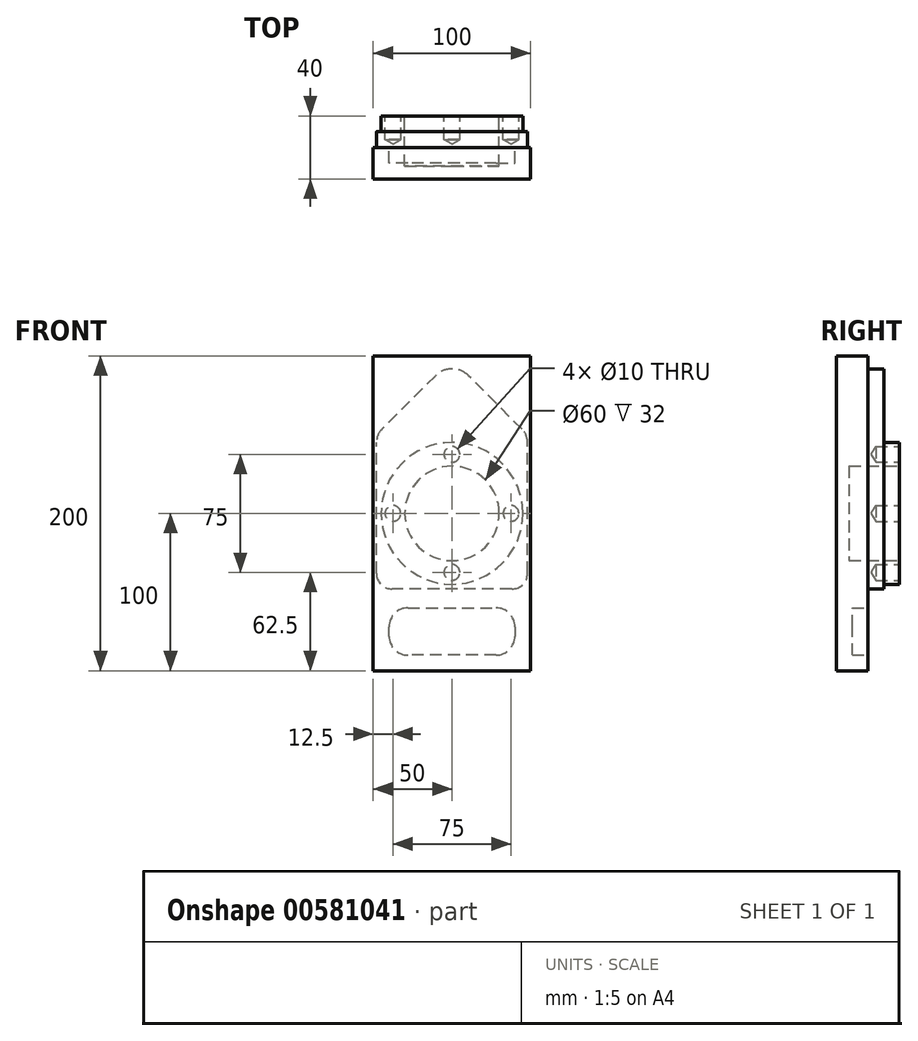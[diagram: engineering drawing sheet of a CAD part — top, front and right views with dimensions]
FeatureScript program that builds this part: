
annotation { "Feature Type Name" : "Feature", "Feature Type Description" : "" }
export const myFeature = defineFeature(function(context is Context, id is Id, definition is map)
    precondition{}
    {
        {
            var Q0;
            Q0=qCreatedBy(makeId("Front.planeOp"),FACE);
            var sketch = newSketch(context, id + "F0", { "sketchPlane" : qUnion([Q0])});
            skLineSegment(sketch, "E0.bottom", {"start": v(50, -100) * mm, "end": v(-50, -100) * mm});
            skLineSegment(sketch, "E0.top", {"start": v(50, 100) * mm, "end": v(-50, 100) * mm});
            skLineSegment(sketch, "E0.left", {"start": v(50, -100) * mm, "end": v(50, 100) * mm});
            skLineSegment(sketch, "E0.right", {"start": v(-50, -100) * mm, "end": v(-50, 100) * mm});
            skPoint(sketch, "E0.middle", {"position": v(0, 0) * mm});
            skSolve(sketch);
        }
        {
            var Q0;
            Q0=makeQuery(id+"F0.imprint","IMPRINT",FACE,{"disambiguationData":[TD([[makeQuery(id+"F0.imprint","IMPRINT",EDGE,{"derivedFrom":sQuery(id+"F0.wireOp",EDGE,"E0.bottom")}),-1.0]])]});
            extrude(context, id + "F1", {"entities" : qUnion([Q0]), "depth" : 20 * mm, "offsetDistance" : 25 * mm});
        }
        {
            var Q0;
            Q0=makeQuery(id+"F1.opExtrude","CAP_FACE",FACE,{"disambiguationData":[OSD([sQuery(id+"F0.wireOp",EDGE,"E0.bottom"),sQuery(id+"F0.wireOp",EDGE,"E0.top"),sQuery(id+"F0.wireOp",EDGE,"E0.left"),sQuery(id+"F0.wireOp",EDGE,"E0.right")])],"isStart":true});
            var sketch = newSketch(context, id + "F2", { "sketchPlane" : qUnion([Q0])});
            skLineSegment(sketch, "E1", {"start": v(-40, -72) * mm, "end": v(-40, -78) * mm});
            skLineSegment(sketch, "E2", {"start": v(-28, -90) * mm, "end": v(28, -90) * mm});
            skLineSegment(sketch, "E3", {"start": v(40, -78) * mm, "end": v(40, -72) * mm});
            skLineSegment(sketch, "E4", {"start": v(28, -60) * mm, "end": v(-28, -60) * mm});
            skArc(sketch, "E5", {"start": v(28, -90) * mm, "mid": v(36.49, -86.49) * mm, "end": v(40, -78) * mm});
            skArc(sketch, "E6", {"start": v(40, -72) * mm, "mid": v(36.49, -63.51) * mm, "end": v(28, -60) * mm});
            skArc(sketch, "E7", {"start": v(-40, -78) * mm, "mid": v(-36.49, -86.49) * mm, "end": v(-28, -90) * mm});
            skArc(sketch, "E8", {"start": v(-28, -60) * mm, "mid": v(-36.49, -63.51) * mm, "end": v(-40, -72) * mm});
            skSolve(sketch);
        }
        {
            var Q0;
            Q0 = qSketchRegion(id + "F2", true);
            extrude(context, id + "F3", {"entities" : qUnion([Q0]), "operationType" : NewBodyOperationType.REMOVE, "oppositeDirection" : true, "depth" : 10 * mm, "offsetDistance" : 25 * mm});
        }
        {
            var Q0;
            Q0=makeQuery(id+"F1.opExtrude","CAP_FACE",FACE,{"disambiguationData":[OSD([sQuery(id+"F0.wireOp",EDGE,"E0.bottom"),sQuery(id+"F0.wireOp",EDGE,"E0.top"),sQuery(id+"F0.wireOp",EDGE,"E0.left"),sQuery(id+"F0.wireOp",EDGE,"E0.right")])],"isStart":true});
            var sketch = newSketch(context, id + "F4", { "sketchPlane" : qUnion([Q0])});
            skLineSegment(sketch, "E9", {"start": v(-48, -38) * mm, "end": v(-48, 45.03) * mm});
            skLineSegment(sketch, "E10", {"start": v(-38, -48) * mm, "end": v(38, -48) * mm});
            skLineSegment(sketch, "E11", {"start": v(48, -38) * mm, "end": v(48, 45.03) * mm});
            skLineSegment(sketch, "E12", {"start": v(-44.49, 53.51) * mm, "end": v(-10.6, 87.4) * mm});
            skLineSegment(sketch, "E13", {"start": v(10.6, 87.4) * mm, "end": v(44.49, 53.51) * mm});
            skArc(sketch, "E14", {"start": v(-48, -38) * mm, "mid": v(-45.07, -45.07) * mm, "end": v(-38, -48) * mm});
            skArc(sketch, "E15", {"start": v(-44.49, 53.51) * mm, "mid": v(-47.09, 49.62) * mm, "end": v(-48, 45.03) * mm});
            skArc(sketch, "E16", {"start": v(10.6, 87.4) * mm, "mid": v(0, 91.79) * mm, "end": v(-10.6, 87.4) * mm});
            skArc(sketch, "E17", {"start": v(48, 45.03) * mm, "mid": v(47.09, 49.62) * mm, "end": v(44.49, 53.51) * mm});
            skArc(sketch, "E18", {"start": v(38, -48) * mm, "mid": v(45.07, -45.07) * mm, "end": v(48, -38) * mm});
            skSolve(sketch);
        }
        {
            var Q0;
            Q0 = qSketchRegion(id + "F4", true);
            extrude(context, id + "F5", {"entities" : qUnion([Q0]), "operationType" : NewBodyOperationType.ADD, "depth" : 10 * mm, "offsetDistance" : 25 * mm});
        }
        {
            var Q0;
            Q0=makeQuery(id+"F5.opExtrude","CAP_FACE",FACE,{"disambiguationData":[OSD([sQuery(id+"F4.wireOp",EDGE,"E9"),sQuery(id+"F4.wireOp",EDGE,"E10"),sQuery(id+"F4.wireOp",EDGE,"E11"),sQuery(id+"F4.wireOp",EDGE,"E12"),sQuery(id+"F4.wireOp",EDGE,"E13"),sQuery(id+"F4.wireOp",EDGE,"E14"),sQuery(id+"F4.wireOp",EDGE,"E15"),sQuery(id+"F4.wireOp",EDGE,"E16"),sQuery(id+"F4.wireOp",EDGE,"E17"),sQuery(id+"F4.wireOp",EDGE,"E18")])],"isStart":false});
            var sketch = newSketch(context, id + "F6", { "sketchPlane" : qUnion([Q0])});
            skCircle(sketch, "E19", {"center": v(0, 0) * mm, "radius": 45 * mm});
            skCircle(sketch, "E20", {"center": v(0, 0) * mm, "radius": 30 * mm});
            skSolve(sketch);
        }
        {
            var Q0;
            Q0 = qSketchRegion(id + "F6", true);
            var Q1;
            Q1=makeQuery(id+"F6.imprint","IMPRINT",FACE,{"disambiguationData":[TD([[makeQuery(id+"F6.imprint","IMPRINT",EDGE,{"derivedFrom":sQuery(id+"F6.wireOp",EDGE,"E20")}),1.0]])]});
            extrude(context, id + "F7", {"entities" : qUnion([Q0, Q1]), "operationType" : NewBodyOperationType.ADD, "depth" : 10 * mm, "offsetDistance" : 25 * mm});
        }
        {
            var Q0;
            Q0=makeQuery(id+"F7.opExtrude","CAP_FACE",FACE,{"disambiguationData":[OSD([sQuery(id+"F6.wireOp",EDGE,"E19")])],"isStart":false});
            var sketch = newSketch(context, id + "F8", { "sketchPlane" : qUnion([Q0])});
            skCircle(sketch, "E21", {"center": v(0, 0) * mm, "radius": 30 * mm});
            skSolve(sketch);
        }
        {
            var Q0;
            Q0 = qSketchRegion(id + "F8", true);
            extrude(context, id + "F9", {"entities" : qUnion([Q0]), "operationType" : NewBodyOperationType.REMOVE, "oppositeDirection" : true, "depth" : 32 * mm, "offsetDistance" : 25 * mm});
        }
        {
            var Q0;
            Q0=makeQuery(id+"F7.opExtrude","CAP_FACE",FACE,{"disambiguationData":[OSD([sQuery(id+"F6.wireOp",EDGE,"E19")])],"isStart":false});
            var sketch = newSketch(context, id + "F10", { "sketchPlane" : qUnion([Q0])});
            skCircle(sketch, "E22", {"center": v(-37.5, 0) * mm, "radius": 5 * mm});
            skCircle(sketch, "E23", {"center": v(0, -37.5) * mm, "radius": 5 * mm});
            skCircle(sketch, "E24", {"center": v(0, 37.5) * mm, "radius": 5 * mm});
            skCircle(sketch, "E25", {"center": v(37.5, 0) * mm, "radius": 5 * mm});
            skCircle(sketch, "E26", {"center": v(0, 0) * mm, "radius": 37.5 * mm, "construction": true});
            skSolve(sketch);
        }
        {
            var Q0;
            Q0=sQuery(id+"F10.wireOp",VERTEX,"E22.center");
            var Q1;
            Q1=sQuery(id+"F10.wireOp",VERTEX,"E24.center");
            var Q2;
            Q2=sQuery(id+"F10.wireOp",VERTEX,"E23.center");
            var Q3;
            Q3=sQuery(id+"F10.wireOp",VERTEX,"E25.center");
            var Q4;
            Q4=makeQuery(id+"F1.opExtrude","SWEPT_BODY",BODY,{"disambiguationData":[OSD([sQuery(id+"F0.wireOp",EDGE,"E0.bottom"),sQuery(id+"F0.wireOp",EDGE,"E0.top"),sQuery(id+"F0.wireOp",EDGE,"E0.left"),sQuery(id+"F0.wireOp",EDGE,"E0.right")])]});
            hole(context, id + "F11", {"style" : HoleStyle.SIMPLE, "endStyle" : HoleEndStyle.BLIND, "holeDiameter" : 10 * mm, "majorDiameter" : 5 * mm, "holeDepth" : 15 * mm, "isTappedThrough" : true, "tappedDepth" : 12 * mm, "tapClearance" : 3, "locations" : qUnion([Q0, Q1, Q2, Q3]), "scope" : qUnion([Q4])});
        }
    });
